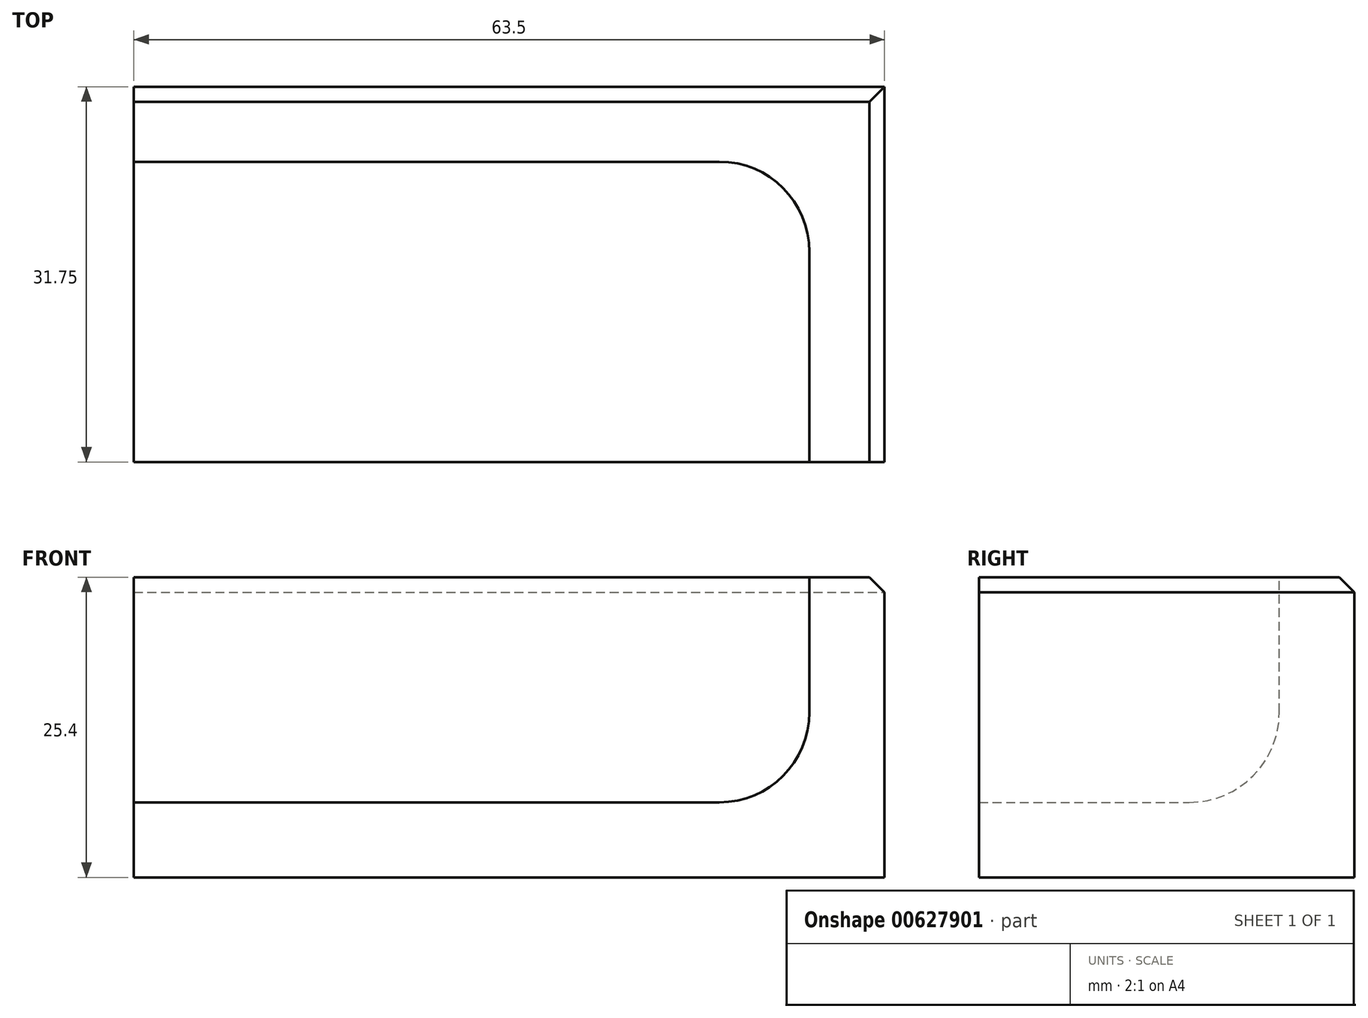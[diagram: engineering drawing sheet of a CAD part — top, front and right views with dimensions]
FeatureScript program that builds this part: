
annotation { "Feature Type Name" : "Feature", "Feature Type Description" : "" }
export const myFeature = defineFeature(function(context is Context, id is Id, definition is map)
    precondition{}
    {
        {
            var Q0;
            Q0=qCreatedBy(makeId("Top.planeOp"),FACE);
            var sketch = newSketch(context, id + "F0", { "sketchPlane" : qUnion([Q0])});
            skLineSegment(sketch, "E0.bottom", {"start": v(0, 0) * mm, "end": v(63.5, 0) * mm});
            skLineSegment(sketch, "E0.top", {"start": v(0, 31.75) * mm, "end": v(63.5, 31.75) * mm});
            skLineSegment(sketch, "E0.left", {"start": v(0, 0) * mm, "end": v(0, 31.75) * mm});
            skLineSegment(sketch, "E0.right", {"start": v(63.5, 0) * mm, "end": v(63.5, 31.75) * mm});
            skSolve(sketch);
        }
        {
            var Q0;
            Q0=makeQuery(id+"F0.imprint","IMPRINT",FACE,{"disambiguationData":[TD([[makeQuery(id+"F0.imprint","IMPRINT",EDGE,{"derivedFrom":sQuery(id+"F0.wireOp",EDGE,"E0.bottom")}),1.0]])]});
            extrude(context, id + "F1", {"entities" : qUnion([Q0]), "depth" : 25.4 * mm, "offsetDistance" : 25.4 * mm});
        }
        {
            var Q0;
            Q0=makeQuery(id+"F1.opExtrude","CAP_FACE",FACE,{"disambiguationData":[OSD([sQuery(id+"F0.wireOp",EDGE,"E0.bottom"),sQuery(id+"F0.wireOp",EDGE,"E0.top"),sQuery(id+"F0.wireOp",EDGE,"E0.left"),sQuery(id+"F0.wireOp",EDGE,"E0.right")])],"isStart":false});
            var sketch = newSketch(context, id + "F2", { "sketchPlane" : qUnion([Q0])});
            skLineSegment(sketch, "E1.bottom", {"start": v(0, 0) * mm, "end": v(57.15, 0) * mm});
            skLineSegment(sketch, "E1.top", {"start": v(0, 25.4) * mm, "end": v(57.15, 25.4) * mm});
            skLineSegment(sketch, "E1.left", {"start": v(0, 0) * mm, "end": v(0, 25.4) * mm});
            skLineSegment(sketch, "E1.right", {"start": v(57.15, 0) * mm, "end": v(57.15, 25.4) * mm});
            skSolve(sketch);
        }
        {
            var Q0;
            Q0 = qSketchRegion(id + "F2", true);
            var Q1;
            Q1=makeQuery(id+"F2.imprint","IMPRINT",FACE,{"disambiguationData":[TD([[makeQuery(id+"F2.imprint","IMPRINT",EDGE,{"derivedFrom":sQuery(id+"F2.wireOp",EDGE,"E1.bottom")}),1.0]])]});
            extrude(context, id + "F3", {"entities" : qUnion([Q0, Q1]), "operationType" : NewBodyOperationType.REMOVE, "oppositeDirection" : true, "depth" : 19.05 * mm, "offsetDistance" : 25.4 * mm});
        }
        {
            var Q0;
            Q0=makeQuery(id+"F3.boolean.opBoolean","COPY",EDGE,{"derivedFrom":makeQuery(id+"F3.opExtrude","CAP_EDGE",EDGE,{"disambiguationData":[OSD([sQuery(id+"F2.wireOp",EDGE,"E1.top")])],"isStart":false})});
            var Q1;
            Q1=makeQuery(id+"F3.boolean.opBoolean","COPY",EDGE,{"derivedFrom":makeQuery(id+"F3.opExtrude","CAP_EDGE",EDGE,{"disambiguationData":[OSD([sQuery(id+"F2.wireOp",EDGE,"E1.right")])],"isStart":false})});
            var Q2;
            Q2=makeQuery(id+"F3.boolean.opBoolean","COPY",EDGE,{"derivedFrom":makeQuery(id+"F3.opExtrude","SWEPT_EDGE",EDGE,{"disambiguationData":[OSD([sQuery(id+"F2.wireOp",EDGE,"E1.top"),sQuery(id+"F2.wireOp",EDGE,"E1.right")])]})});
            fillet(context, id + "F4", {"entities" : qUnion([Q0, Q1, Q2]), "radius" : 7.62 * mm, "tangentPropagation" : true, "allowEdgeOverflow" : false});
        }
        {
            var Q0;
            Q0=makeQuery(id+"F1.opExtrude","CAP_EDGE",EDGE,{"disambiguationData":[OSD([sQuery(id+"F0.wireOp",EDGE,"E0.right")])],"isStart":false});
            var Q1;
            Q1=makeQuery(id+"F1.opExtrude","CAP_EDGE",EDGE,{"disambiguationData":[OSD([sQuery(id+"F0.wireOp",EDGE,"E0.top")])],"isStart":false});
            chamfer(context, id + "F5", {"entities" : qUnion([Q0, Q1]), "width" : 1.27 * mm, "tangentPropagation" : true});
        }
    });
